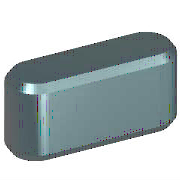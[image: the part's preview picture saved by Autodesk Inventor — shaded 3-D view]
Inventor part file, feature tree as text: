
AUTODESK INVENTOR PART (.ipt)
format: ipt  version: 2015 (Build 190159000, 159)  size: 134,656 bytes
history: native  units: mm (DEFAULTED — no unit token found)
features: plane x3, extrude x1
ambient origin geometry x8: Origin, YZ Plane, XZ Plane, XY Plane, X Axis, Y Axis, Z Axis, Center Point
bodies: Solid1 (feature_tree)
feature tree (4):
  plane  "Work Plane1"
  plane  "Work Plane2"
  extrude  "轴承体1"  Depth=3.0mm
  plane  "Work Plane3"
